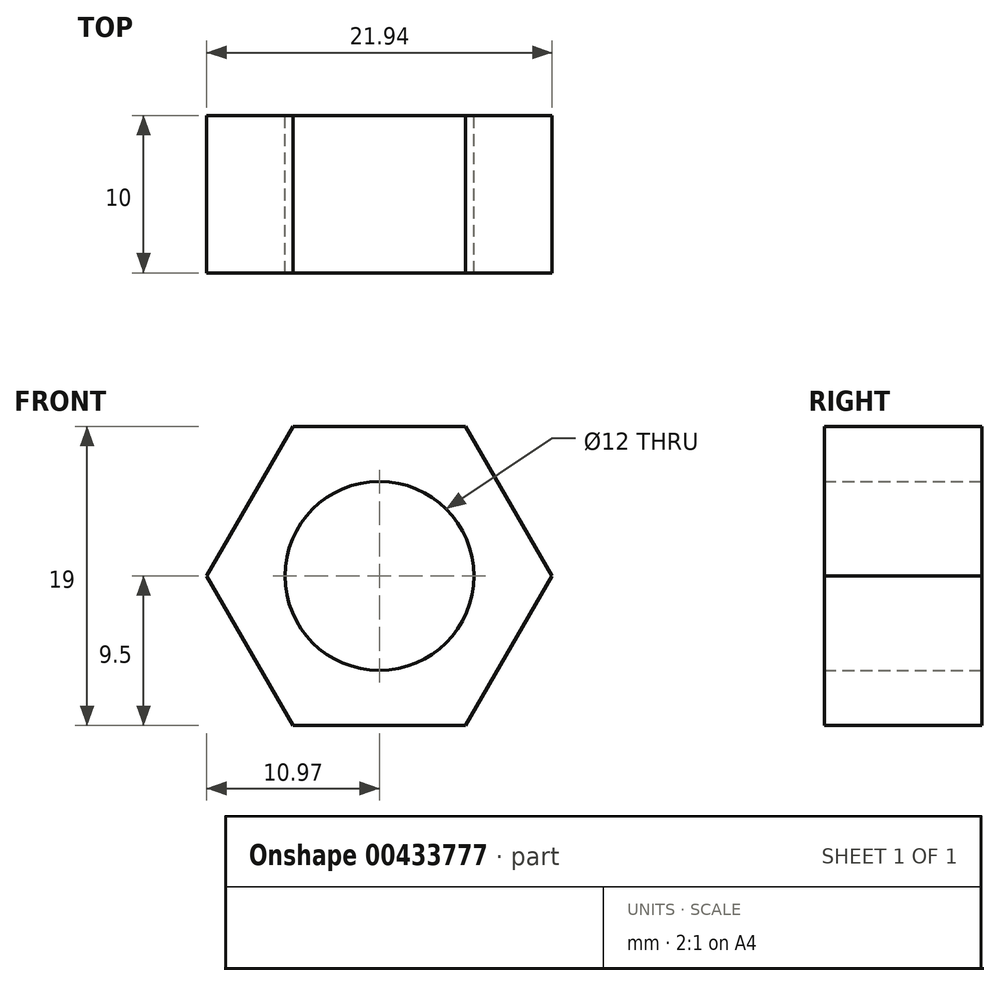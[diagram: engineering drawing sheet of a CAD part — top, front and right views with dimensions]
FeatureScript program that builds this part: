
annotation { "Feature Type Name" : "Feature", "Feature Type Description" : "" }
export const myFeature = defineFeature(function(context is Context, id is Id, definition is map)
    precondition{}
    {
        {
            var Q0;
            Q0=qCreatedBy(makeId("Front.planeOp"),FACE);
            var sketch = newSketch(context, id + "F0", { "sketchPlane" : qUnion([Q0])});
            skLineSegment(sketch, "E0", {"start": v(0, 9.5) * mm, "end": v(-5.48, 9.5) * mm});
            skLineSegment(sketch, "E1", {"start": v(-5.48, 9.5) * mm, "end": v(-10.97, 0) * mm});
            skLineSegment(sketch, "E2", {"start": v(0, 9.5) * mm, "end": v(0, 0) * mm, "construction": true});
            skLineSegment(sketch, "E3.MirrorCS", {"start": v(5.48, 9.5) * mm, "end": v(10.97, 0) * mm});
            skLineSegment(sketch, "E4.MirrorCS", {"start": v(0, 9.5) * mm, "end": v(5.48, 9.5) * mm});
            skLineSegment(sketch, "E5", {"start": v(0, 0) * mm, "end": v(10.97, 0) * mm, "construction": true});
            skLineSegment(sketch, "E6", {"start": v(0, 0) * mm, "end": v(8.23, 4.75) * mm, "construction": true});
            skLineSegment(sketch, "E7.MirrorCS", {"start": v(5.48, -9.5) * mm, "end": v(10.97, 0) * mm});
            skLineSegment(sketch, "E8.MirrorCS", {"start": v(0, -9.5) * mm, "end": v(5.48, -9.5) * mm});
            skLineSegment(sketch, "E9.MirrorCS", {"start": v(0, -9.5) * mm, "end": v(-5.48, -9.5) * mm});
            skLineSegment(sketch, "E10.MirrorCS", {"start": v(-5.48, -9.5) * mm, "end": v(-10.97, 0) * mm});
            skCircle(sketch, "E11", {"center": v(0, 0) * mm, "radius": 6 * mm});
            skSolve(sketch);
        }
        {
            var Q0;
            Q0 = qSketchRegion(id + "F0", true);
            extrude(context, id + "F1", {"entities" : qUnion([Q0]), "depth" : 10 * mm});
        }
    });
